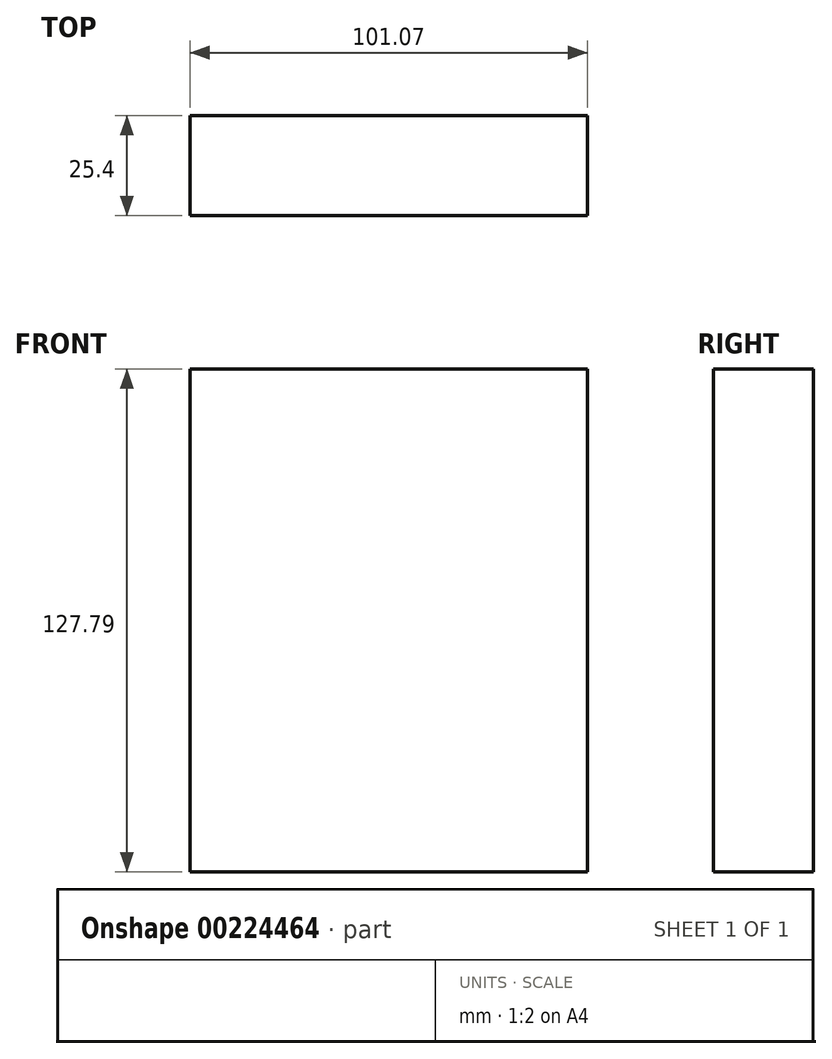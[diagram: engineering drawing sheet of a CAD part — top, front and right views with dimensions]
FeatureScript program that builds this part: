
annotation { "Feature Type Name" : "Feature", "Feature Type Description" : "" }
export const myFeature = defineFeature(function(context is Context, id is Id, definition is map)
    precondition{}
    {
        {
            var Q0;
            Q0=qCreatedBy(makeId("Front.planeOp"),FACE);
            var sketch = newSketch(context, id + "F0", { "sketchPlane" : qUnion([Q0])});
            skLineSegment(sketch, "E0.bottom", {"start": v(-39.93, 80.42) * mm, "end": v(61.14, 80.42) * mm});
            skLineSegment(sketch, "E0.top", {"start": v(-39.93, -47.37) * mm, "end": v(61.14, -47.37) * mm});
            skLineSegment(sketch, "E0.left", {"start": v(-39.93, 80.42) * mm, "end": v(-39.93, -47.37) * mm});
            skLineSegment(sketch, "E0.right", {"start": v(61.14, 80.42) * mm, "end": v(61.14, -47.37) * mm});
            skSolve(sketch);
        }
        {
            var Q0;
            Q0 = qSketchRegion(id + "F0", true);
            extrude(context, id + "F1", {"entities" : qUnion([Q0]), "depth" : 25.4 * mm});
        }
    });
